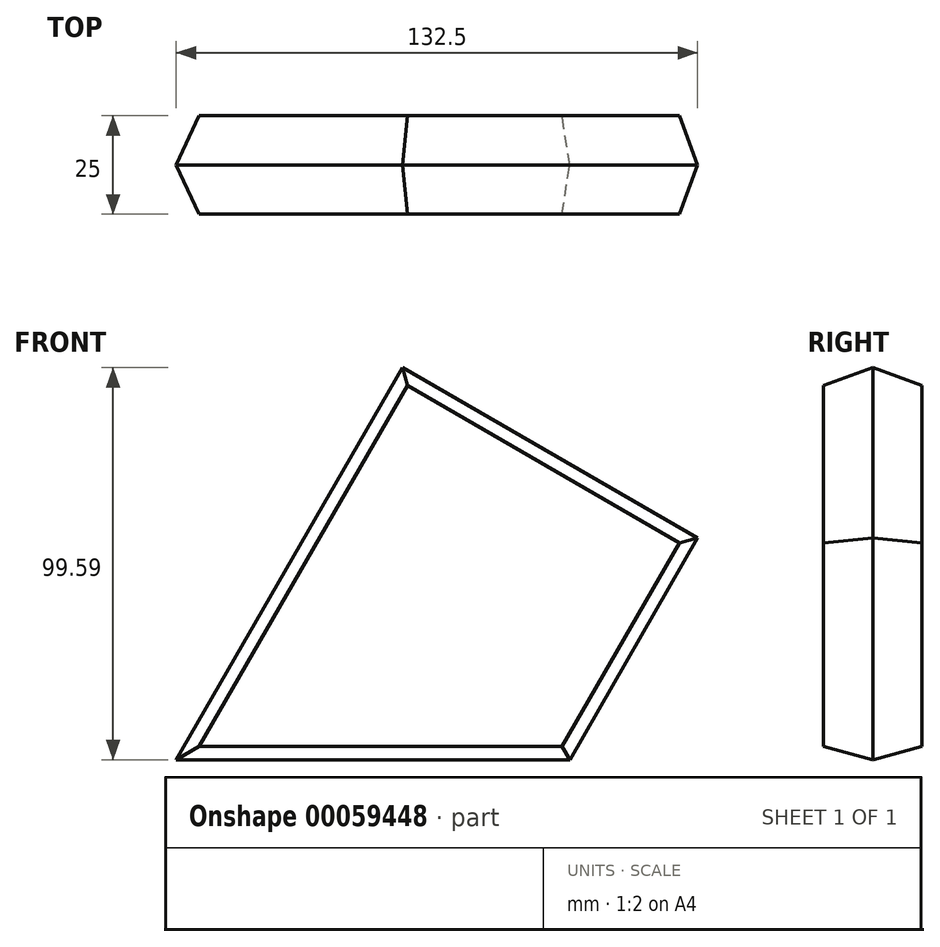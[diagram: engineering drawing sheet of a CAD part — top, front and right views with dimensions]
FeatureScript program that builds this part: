
annotation { "Feature Type Name" : "Feature", "Feature Type Description" : "" }
export const myFeature = defineFeature(function(context is Context, id is Id, definition is map)
    precondition{}
    {
        {
            var Q0;
            Q0=qCreatedBy(makeId("Front.planeOp"),FACE);
            var sketch = newSketch(context, id + "F0", { "sketchPlane" : qUnion([Q0])});
            skLineSegment(sketch, "E0", {"start": v(0, 0) * mm, "end": v(100, 0) * mm});
            skLineSegment(sketch, "E1", {"start": v(100, 0) * mm, "end": v(132.5, 56.3) * mm});
            skLineSegment(sketch, "E2", {"start": v(132.5, 56.3) * mm, "end": v(57.5, 99.6) * mm});
            skLineSegment(sketch, "E3", {"start": v(57.5, 99.6) * mm, "end": v(0, 0) * mm});
            skSolve(sketch);
        }
        {
            var Q0;
            Q0=makeQuery(id+"F0.imprint","IMPRINT",FACE,{"disambiguationData":[TD([[makeQuery(id+"F0.imprint","IMPRINT",EDGE,{"derivedFrom":sQuery(id+"F0.wireOp",EDGE,"E0")}),1.0]])]});
            extrude(context, id + "F1", {"entities" : qUnion([Q0]), "endBound" : BoundingType.SYMMETRIC, "depth" : 25 * mm, "hasDraft" : true, "draftAngle" : 15 * degree, "draftPullDirection" : true});
        }
    });
